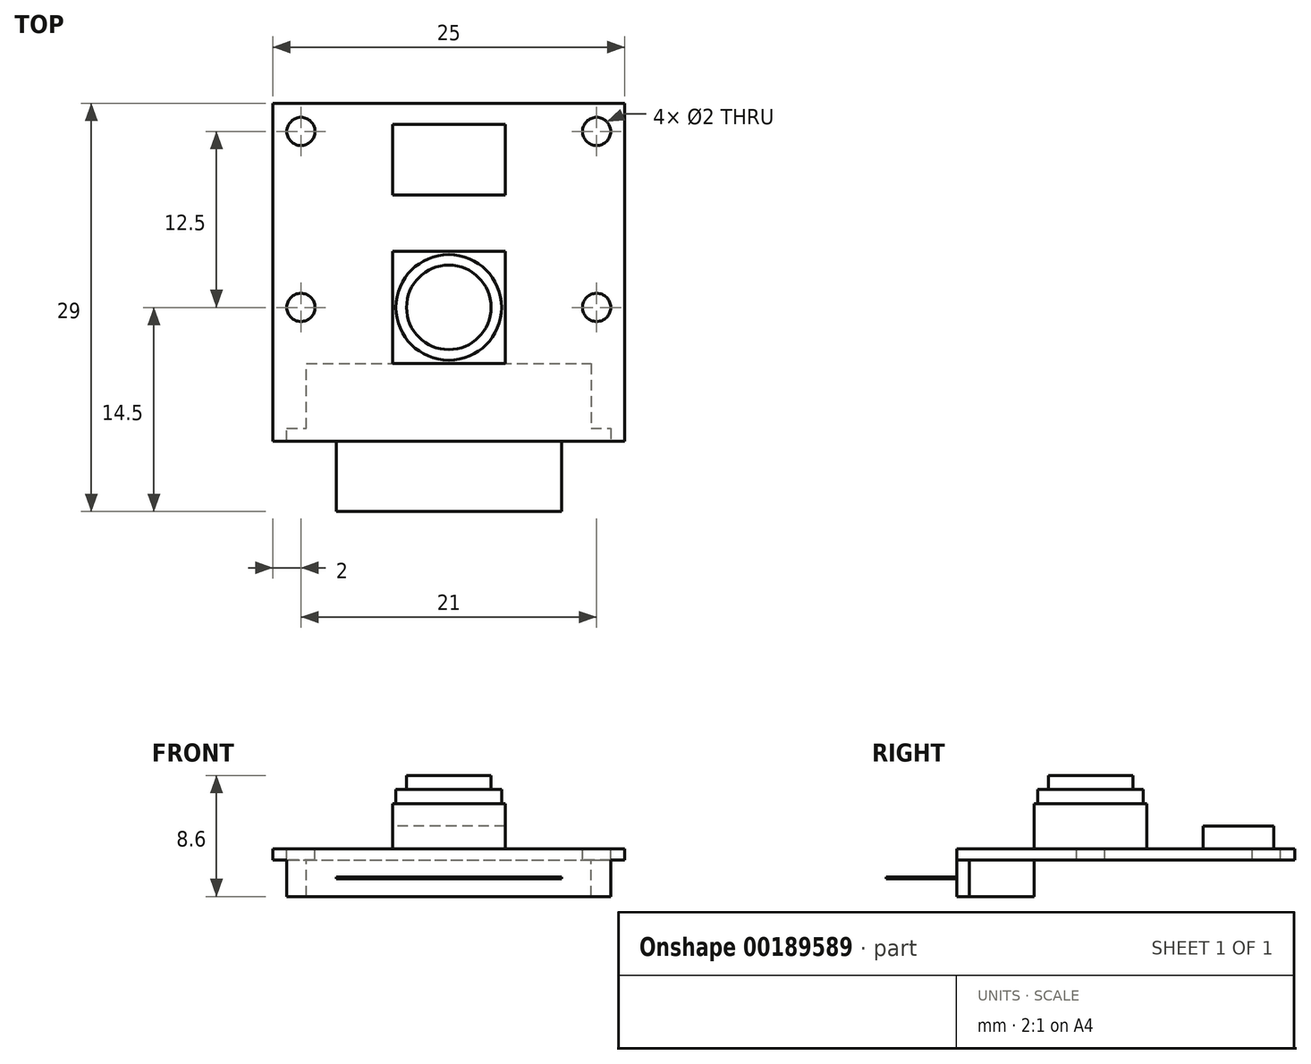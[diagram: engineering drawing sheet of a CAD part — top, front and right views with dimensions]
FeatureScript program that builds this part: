
annotation { "Feature Type Name" : "Feature", "Feature Type Description" : "" }
export const myFeature = defineFeature(function(context is Context, id is Id, definition is map)
    precondition{}
    {
        {
            var Q0;
            Q0=qCreatedBy(makeId("Top.planeOp"),FACE);
            var sketch = newSketch(context, id + "F0", { "sketchPlane" : qUnion([Q0])});
            skLineSegment(sketch, "E0.bottom", {"start": v(-12.5, 14.5) * mm, "end": v(12.5, 14.5) * mm});
            skLineSegment(sketch, "E0.top", {"start": v(-12.5, -9.5) * mm, "end": v(12.5, -9.5) * mm});
            skLineSegment(sketch, "E0.left", {"start": v(-12.5, 14.5) * mm, "end": v(-12.5, -9.5) * mm});
            skLineSegment(sketch, "E0.right", {"start": v(12.5, 14.5) * mm, "end": v(12.5, -9.5) * mm});
            skSolve(sketch);
        }
        {
            var Q0;
            Q0=qSketchRegion(id+"F0",true);
            extrude(context, id + "F1", {"entities" : qUnion([Q0]), "oppositeDirection" : true, "depth" : .8 * mm});
        }
        {
            var Q0;
            Q0=makeQuery(id+"F1.opExtrude","CAP_FACE",FACE,{"disambiguationData":[OSD([sQuery(id+"F0.wireOp",EDGE,"E0.bottom"),sQuery(id+"F0.wireOp",EDGE,"E0.top"),sQuery(id+"F0.wireOp",EDGE,"E0.left"),sQuery(id+"F0.wireOp",EDGE,"E0.right")])],"isStart":true});
            var sketch = newSketch(context, id + "F2", { "sketchPlane" : qUnion([Q0])});
            skLineSegment(sketch, "E1.rect.bottom", {"start": v(4, 4) * mm, "end": v(-4, 4) * mm});
            skLineSegment(sketch, "E1.rect.top", {"start": v(4, -4) * mm, "end": v(-4, -4) * mm});
            skLineSegment(sketch, "E1.rect.left", {"start": v(4, 4) * mm, "end": v(4, -4) * mm});
            skLineSegment(sketch, "E1.rect.right", {"start": v(-4, 4) * mm, "end": v(-4, -4) * mm});
            skPoint(sketch, "E1.rect.middle", {"position": v(0, 0) * mm});
            skSolve(sketch);
        }
        {
            var Q0;
            Q0=qSketchRegion(id+"F2",true);
            extrude(context, id + "F3", {"entities" : qUnion([Q0]), "operationType" : NewBodyOperationType.ADD, "depth" : 3.2 * mm});
        }
        {
            var Q0;
            Q0=makeQuery(id+"F3.opExtrude","CAP_FACE",FACE,{"disambiguationData":[OSD([sQuery(id+"F2.wireOp",EDGE,"E1.rect.bottom"),sQuery(id+"F2.wireOp",EDGE,"E1.rect.top"),sQuery(id+"F2.wireOp",EDGE,"E1.rect.left"),sQuery(id+"F2.wireOp",EDGE,"E1.rect.right")])],"isStart":false});
            var sketch = newSketch(context, id + "F4", { "sketchPlane" : qUnion([Q0])});
            skCircle(sketch, "E2", {"center": v(0, 0) * mm, "radius": 3.75 * mm});
            skSolve(sketch);
        }
        {
            var Q0;
            Q0=qSketchRegion(id+"F4",true);
            var Q1;
            Q1=sQuery(id+"F4.wireOp",EDGE,"E2");
            extrude(context, id + "F5", {"entities" : qUnion([Q0]), "operationType" : NewBodyOperationType.ADD, "surfaceEntities" : qUnion([Q1]), "depth" : 1 * mm});
        }
        {
            var Q0;
            Q0=makeQuery(id+"F5.opExtrude","CAP_FACE",FACE,{"disambiguationData":[OSD([sQuery(id+"F4.wireOp",EDGE,"E2")])],"isStart":false});
            var sketch = newSketch(context, id + "F6", { "sketchPlane" : qUnion([Q0])});
            skCircle(sketch, "E3", {"center": v(0, 0) * mm, "radius": 3 * mm});
            skSolve(sketch);
        }
        {
            var Q0;
            Q0=qSketchRegion(id+"F6",true);
            extrude(context, id + "F7", {"entities" : qUnion([Q0]), "operationType" : NewBodyOperationType.ADD, "depth" : 1 * mm});
        }
        {
            var Q0;
            Q0=makeQuery(id+"F1.opExtrude","CAP_FACE",FACE,{"disambiguationData":[OSD([sQuery(id+"F0.wireOp",EDGE,"E0.bottom"),sQuery(id+"F0.wireOp",EDGE,"E0.top"),sQuery(id+"F0.wireOp",EDGE,"E0.left"),sQuery(id+"F0.wireOp",EDGE,"E0.right")])],"isStart":true});
            var sketch = newSketch(context, id + "F8", { "sketchPlane" : qUnion([Q0])});
            skPoint(sketch, "E4", {"position": v(-10.5, 12.5) * mm});
            skPoint(sketch, "E5", {"position": v(10.5, 12.5) * mm});
            skPoint(sketch, "E6", {"position": v(10.5, 0) * mm});
            skPoint(sketch, "E7", {"position": v(-10.5, 0) * mm});
            skSolve(sketch);
        }
        {
            var Q0;
            Q0=sQuery(id+"F8.wireOp",VERTEX,"E4");
            var Q1;
            Q1=sQuery(id+"F8.wireOp",VERTEX,"E5");
            var Q2;
            Q2=sQuery(id+"F8.wireOp",VERTEX,"E6");
            var Q3;
            Q3=sQuery(id+"F8.wireOp",VERTEX,"E7");
            var Q4;
            Q4=makeQuery(id+"F1.opExtrude","SWEPT_BODY",BODY,{"disambiguationData":[OSD([sQuery(id+"F0.wireOp",EDGE,"E0.bottom"),sQuery(id+"F0.wireOp",EDGE,"E0.top"),sQuery(id+"F0.wireOp",EDGE,"E0.left"),sQuery(id+"F0.wireOp",EDGE,"E0.right")])]});
            hole(context, id + "F9", {"style" : HoleStyle.SIMPLE, "holeDiameter" : 2 * mm, "endStyle" : HoleEndStyle.THROUGH, "locations" : qUnion([Q0, Q1, Q2, Q3]), "scope" : qUnion([Q4])});
        }
        {
            var Q0;
            Q0=makeQuery(id+"F1.opExtrude","CAP_FACE",FACE,{"disambiguationData":[OSD([sQuery(id+"F0.wireOp",EDGE,"E0.bottom"),sQuery(id+"F0.wireOp",EDGE,"E0.top"),sQuery(id+"F0.wireOp",EDGE,"E0.left"),sQuery(id+"F0.wireOp",EDGE,"E0.right")])],"isStart":true});
            var sketch = newSketch(context, id + "F10", { "sketchPlane" : qUnion([Q0])});
            skLineSegment(sketch, "E8.bottom", {"start": v(4, 8) * mm, "end": v(-4, 8) * mm});
            skLineSegment(sketch, "E8.top", {"start": v(4, 13) * mm, "end": v(-4, 13) * mm});
            skLineSegment(sketch, "E8.left", {"start": v(4, 8) * mm, "end": v(4, 13) * mm});
            skLineSegment(sketch, "E8.right", {"start": v(-4, 8) * mm, "end": v(-4, 13) * mm});
            skSolve(sketch);
        }
        {
            var Q0;
            Q0=qSketchRegion(id+"F10",true);
            extrude(context, id + "F11", {"entities" : qUnion([Q0]), "operationType" : NewBodyOperationType.ADD, "depth" : 1.6 * mm});
        }
        {
            var Q0;
            Q0=makeQuery(id+"F1.opExtrude","CAP_FACE",FACE,{"disambiguationData":[OSD([sQuery(id+"F0.wireOp",EDGE,"E0.bottom"),sQuery(id+"F0.wireOp",EDGE,"E0.top"),sQuery(id+"F0.wireOp",EDGE,"E0.left"),sQuery(id+"F0.wireOp",EDGE,"E0.right")])],"isStart":false});
            var sketch = newSketch(context, id + "F12", { "sketchPlane" : qUnion([Q0])});
            skLineSegment(sketch, "E9", {"start": v(-11.5, 9.5) * mm, "end": v(-11.5, 8.6) * mm});
            skLineSegment(sketch, "E10", {"start": v(-11.5, 8.6) * mm, "end": v(-10.1, 8.6) * mm});
            skLineSegment(sketch, "E11", {"start": v(-10.1, 8.6) * mm, "end": v(-10.1, 4) * mm});
            skLineSegment(sketch, "E12", {"start": v(-10.1, 4) * mm, "end": v(10.1, 4) * mm});
            skLineSegment(sketch, "E13", {"start": v(10.1, 4) * mm, "end": v(10.1, 8.6) * mm});
            skLineSegment(sketch, "E14", {"start": v(10.1, 8.6) * mm, "end": v(11.5, 8.6) * mm});
            skLineSegment(sketch, "E15", {"start": v(11.5, 8.6) * mm, "end": v(11.5, 9.5) * mm});
            skLineSegment(sketch, "E16", {"start": v(11.5, 9.5) * mm, "end": v(-11.5, 9.5) * mm});
            skSolve(sketch);
        }
        {
            var Q0;
            Q0=qSketchRegion(id+"F12",true);
            extrude(context, id + "F13", {"entities" : qUnion([Q0]), "operationType" : NewBodyOperationType.ADD, "depth" : 2.6 * mm});
        }
        {
            var Q0;
            Q0=makeQuery(id+"F13.boolean.opBoolean","MERGE",FACE,{"derivedFrom":[makeQuery(id+"F1.opExtrude","SWEPT_FACE",FACE,{"disambiguationData":[OSD([sQuery(id+"F0.wireOp",EDGE,"E0.top")])]}),makeQuery(id+"F13.opExtrude","SWEPT_FACE",FACE,{"disambiguationData":[OSD([sQuery(id+"F12.wireOp",EDGE,"E16")])]})]});
            var sketch = newSketch(context, id + "F14", { "sketchPlane" : qUnion([Q0])});
            skLineSegment(sketch, "E17.bottom", {"start": v(-8, -2) * mm, "end": v(8, -2) * mm});
            skLineSegment(sketch, "E17.top", {"start": v(-8, -2.15) * mm, "end": v(8, -2.15) * mm});
            skLineSegment(sketch, "E17.left", {"start": v(-8, -2) * mm, "end": v(-8, -2.15) * mm});
            skLineSegment(sketch, "E17.right", {"start": v(8, -2) * mm, "end": v(8, -2.15) * mm});
            skSolve(sketch);
        }
        {
            var Q0;
            Q0=qSketchRegion(id+"F14",true);
            extrude(context, id + "F15", {"entities" : qUnion([Q0]), "operationType" : NewBodyOperationType.ADD, "depth" : 5 * mm});
        }
    });
